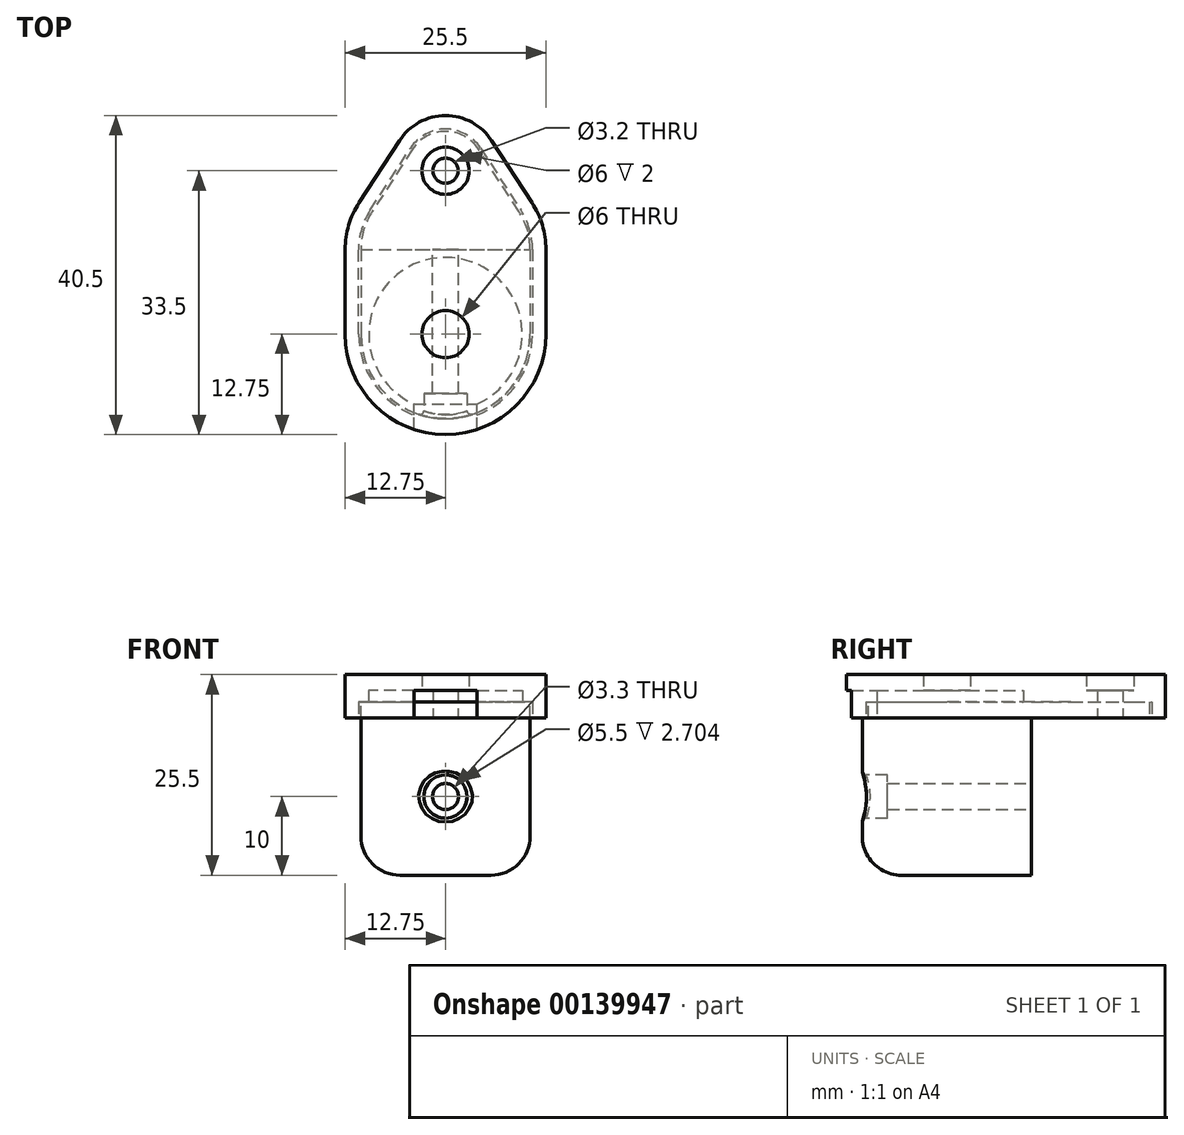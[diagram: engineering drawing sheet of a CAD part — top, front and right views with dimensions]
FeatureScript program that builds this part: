
annotation { "Feature Type Name" : "Feature", "Feature Type Description" : "" }
export const myFeature = defineFeature(function(context is Context, id is Id, definition is map)
    precondition{}
    {
        {
            var Q0;
            Q0=qCreatedBy(makeId("Top.planeOp"),FACE);
            var sketch = newSketch(context, id + "F0", { "sketchPlane" : qUnion([Q0])});
            skCircle(sketch, "E0", {"center": v(0, 0) * mm, "radius": 9.75 * mm, "construction": true});
            skLineSegment(sketch, "E1", {"start": v(-10.75, 10.75) * mm, "end": v(10.75, 10.75) * mm});
            skArc(sketch, "E2", {"start": v(-10.75, 0) * mm, "mid": v(0, -10.75) * mm, "end": v(10.75, 0) * mm});
            skLineSegment(sketch, "E3", {"start": v(-10.75, 10.75) * mm, "end": v(-10.75, 0) * mm});
            skLineSegment(sketch, "E4", {"start": v(10.75, 10.75) * mm, "end": v(10.75, 0) * mm});
            skSolve(sketch);
        }
        {
            var Q0;
            Q0=makeQuery(id+"F0.imprint","IMPRINT",FACE,{"disambiguationData":[TD([[makeQuery(id+"F0.imprint","IMPRINT",EDGE,{"derivedFrom":sQuery(id+"F0.wireOp",EDGE,"E1")}),-1.0]])]});
            extrude(context, id + "F1", {"entities" : qUnion([Q0]), "oppositeDirection" : true, "depth" : 20 * mm});
        }
        {
            var Q0;
            Q0=makeQuery(id+"F1.opExtrude","CAP_FACE",FACE,{"disambiguationData":[OSD([sQuery(id+"F0.wireOp",EDGE,"E1"),sQuery(id+"F0.wireOp",EDGE,"E2"),sQuery(id+"F0.wireOp",EDGE,"E3"),sQuery(id+"F0.wireOp",EDGE,"E4")])],"isStart":true});
            var sketch = newSketch(context, id + "F2", { "sketchPlane" : qUnion([Q0])});
            skArc(sketch, "E5", {"start": v(-10.75, 0) * mm, "mid": v(0, -10.75) * mm, "end": v(10.75, 0) * mm});
            skCircle(sketch, "E6", {"center": v(0, 20.75) * mm, "radius": 1.6 * mm});
            skLineSegment(sketch, "E7", {"start": v(10.75, 0) * mm, "end": v(10.75, 10.75) * mm});
            skLineSegment(sketch, "E8", {"start": v(-10.75, 0) * mm, "end": v(-10.75, 10.75) * mm});
            skArc(sketch, "E9", {"start": v(4.2, 23.47) * mm, "mid": v(0, 25.75) * mm, "end": v(-4.2, 23.47) * mm});
            skArc(sketch, "E10", {"start": v(-9.31, 15.6) * mm, "mid": v(-10.38, 13.28) * mm, "end": v(-10.75, 10.75) * mm});
            skArc(sketch, "E11", {"start": v(10.75, 10.75) * mm, "mid": v(10.38, 13.28) * mm, "end": v(9.31, 15.6) * mm});
            skLineSegment(sketch, "E12", {"start": v(9.31, 15.6) * mm, "end": v(4.2, 23.47) * mm});
            skLineSegment(sketch, "E13", {"start": v(-4.2, 23.47) * mm, "end": v(-9.31, 15.6) * mm});
            skSolve(sketch);
        }
        {
            var Q0;
            Q0 = qSketchRegion(id + "F2", true);
            extrude(context, id + "F3", {"entities" : qUnion([Q0]), "operationType" : NewBodyOperationType.ADD, "depth" : 2 * mm});
        }
        {
            var Q0;
            Q0=makeQuery(id+"F1.opExtrude","SWEPT_FACE",FACE,{"disambiguationData":[OSD([sQuery(id+"F0.wireOp",EDGE,"E1")])]});
            var sketch = newSketch(context, id + "F4", { "sketchPlane" : qUnion([Q0])});
            skCircle(sketch, "E14", {"center": v(0, -10) * mm, "radius": 1.65 * mm});
            skSolve(sketch);
        }
        {
            var Q0;
            Q0 = qSketchRegion(id + "F4", true);
            extrude(context, id + "F5", {"entities" : qUnion([Q0]), "operationType" : NewBodyOperationType.REMOVE, "oppositeDirection" : true, "depth" : 30 * mm});
        }
        {
            var Q0;
            Q0=makeQuery(id+"F1.opExtrude","CAP_EDGE",EDGE,{"disambiguationData":[OSD([sQuery(id+"F0.wireOp",EDGE,"E2")])],"isStart":false});
            cPoint(context, id + "F6", {"entities" : qUnion([Q0]), "parameter" : 0.5});
        }
        {
            var Q0;
            Q0=qCreatedBy(makeId("Front.planeOp"),FACE);
            var Q1;
            Q1 = qCreatedBy(id + "F6" ,VERTEX);
            cPlane(context, id + "F7", {"entities" : qUnion([Q0, Q1]), "cplaneType" : CPlaneType.PLANE_POINT, "offset" : 25 * mm, "width" : 150 * mm, "height" : 150 * mm});
        }
        {
            var Q0;
            Q0=qCreatedBy(id+"F7.planeOp",FACE);
            var sketch = newSketch(context, id + "F8", { "sketchPlane" : qUnion([Q0])});
            skCircle(sketch, "E15", {"center": v(0, -10) * mm, "radius": 2.75 * mm});
            skSolve(sketch);
        }
        {
            var Q0;
            Q0 = qSketchRegion(id + "F8", true);
            extrude(context, id + "F9", {"entities" : qUnion([Q0]), "operationType" : NewBodyOperationType.REMOVE, "oppositeDirection" : true, "depth" : 3.2 * mm});
        }
        {
            var Q0;
            Q0=makeQuery(id+"F9.boolean.opBoolean","INTERSECT",EDGE,{"derivedFrom":[makeQuery(id+"FgSbUSgyND46Qtd_1.boolean.opBoolean","MERGE",FACE,{"derivedFrom":[makeQuery(id+"F3.boolean.opBoolean","MERGE",FACE,{"derivedFrom":[makeQuery(id+"F1.opExtrude","SWEPT_FACE",FACE,{"disambiguationData":[OSD([sQuery(id+"F0.wireOp",EDGE,"E2")])]}),makeQuery(id+"F3.opExtrude","SWEPT_FACE",FACE,{"disambiguationData":[OSD([sQuery(id+"F2.wireOp",EDGE,"do54rNCg-6hwt-ThKP-AdQH-TqJ7PFSLBjPX")])]}),makeQuery(id+"F3.opExtrude","SWEPT_FACE",FACE,{"disambiguationData":[OSD([sQuery(id+"F2.wireOp",EDGE,"E5")])]})]}),makeQuery(id+"FgSbUSgyND46Qtd_1.opExtrude","SWEPT_FACE",FACE,{"disambiguationData":[OSD([sQuery(id+"Fd06qgfGwgJFH88_1.wireOp",EDGE,"OvbUGwiE-2nU8-rEHt-l5LO-rey32bBuKM9T")])]})]}),makeQuery(id+"F9.opExtrude","SWEPT_FACE",FACE,{"disambiguationData":[OSD([sQuery(id+"F8.wireOp",EDGE,"E15")])]})]});
            fillet(context, id + "F10", {"entities" : qUnion([Q0]), "radius" : 0.5 * mm, "tangentPropagation" : true, "allowEdgeOverflow" : false});
        }
        {
            var Q0;
            Q0=makeQuery(id+"F1.opExtrude","CAP_EDGE",EDGE,{"disambiguationData":[OSD([sQuery(id+"F0.wireOp",EDGE,"E2")])],"isStart":false});
            fillet(context, id + "F11", {"entities" : qUnion([Q0]), "radius" : 5 * mm, "tangentPropagation" : true, "allowEdgeOverflow" : false});
        }
        {
            var Q0;
            Q0=qCreatedBy(makeId("Top.planeOp"),FACE);
            var sketch = newSketch(context, id + "F12", { "sketchPlane" : qUnion([Q0])});
            skArc(sketch, "E16", {"start": v(-11.05, 0) * mm, "mid": v(0, -11.05) * mm, "end": v(11.05, 0) * mm});
            skArc(sketch, "E17", {"start": v(-9.57, 15.76) * mm, "mid": v(-10.67, 13.36) * mm, "end": v(-11.05, 10.75) * mm});
            skArc(sketch, "E18", {"start": v(11.05, 10.75) * mm, "mid": v(10.67, 13.36) * mm, "end": v(9.57, 15.76) * mm});
            skArc(sketch, "E19", {"start": v(4.44, 23.64) * mm, "mid": v(0, 26.05) * mm, "end": v(-4.44, 23.64) * mm});
            skLineSegment(sketch, "E20", {"start": v(-11.05, 0) * mm, "end": v(-11.05, 10.75) * mm});
            skLineSegment(sketch, "E21", {"start": v(-9.57, 15.76) * mm, "end": v(-4.44, 23.64) * mm});
            skLineSegment(sketch, "E22", {"start": v(4.44, 23.64) * mm, "end": v(9.57, 15.76) * mm});
            skLineSegment(sketch, "E23", {"start": v(11.05, 10.75) * mm, "end": v(11.05, 0) * mm});
            skArc(sketch, "E24", {"start": v(-12.75, 0) * mm, "mid": v(0, -12.75) * mm, "end": v(12.75, 0) * mm});
            skArc(sketch, "E25", {"start": v(-11, 16.68) * mm, "mid": v(-12.3, 13.84) * mm, "end": v(-12.75, 10.75) * mm});
            skArc(sketch, "E26", {"start": v(12.75, 10.75) * mm, "mid": v(12.3, 13.84) * mm, "end": v(11, 16.68) * mm});
            skArc(sketch, "E27", {"start": v(5.87, 24.56) * mm, "mid": v(0, 27.75) * mm, "end": v(-5.87, 24.56) * mm});
            skLineSegment(sketch, "E28", {"start": v(-12.75, 0) * mm, "end": v(-12.75, 10.75) * mm});
            skLineSegment(sketch, "E29", {"start": v(-11, 16.68) * mm, "end": v(-5.87, 24.56) * mm});
            skLineSegment(sketch, "E30", {"start": v(5.87, 24.56) * mm, "end": v(11, 16.68) * mm});
            skLineSegment(sketch, "E31", {"start": v(12.75, 10.75) * mm, "end": v(12.75, 0) * mm});
            skSolve(sketch);
        }
        {
            var Q0;
            Q0 = qSketchRegion(id + "F12", true);
            extrude(context, id + "F13", {"entities" : qUnion([Q0]), "depth" : 2 * mm});
        }
        {
            var Q0;
            Q0=makeQuery(id+"F13.opExtrude","CAP_FACE",FACE,{"disambiguationData":[OSD([sQuery(id+"F12.wireOp",EDGE,"E16"),sQuery(id+"F12.wireOp",EDGE,"E17"),sQuery(id+"F12.wireOp",EDGE,"E18"),sQuery(id+"F12.wireOp",EDGE,"E19"),sQuery(id+"F12.wireOp",EDGE,"E20"),sQuery(id+"F12.wireOp",EDGE,"E21"),sQuery(id+"F12.wireOp",EDGE,"E22"),sQuery(id+"F12.wireOp",EDGE,"E23"),sQuery(id+"F12.wireOp",EDGE,"E24"),sQuery(id+"F12.wireOp",EDGE,"E25"),sQuery(id+"F12.wireOp",EDGE,"E26"),sQuery(id+"F12.wireOp",EDGE,"E27"),sQuery(id+"F12.wireOp",EDGE,"E28"),sQuery(id+"F12.wireOp",EDGE,"E29"),sQuery(id+"F12.wireOp",EDGE,"E30"),sQuery(id+"F12.wireOp",EDGE,"E31")])],"isStart":false});
            var sketch = newSketch(context, id + "F14", { "sketchPlane" : qUnion([Q0])});
            skCircle(sketch, "E32", {"center": v(0, 20.75) * mm, "radius": 1.6 * mm});
            skArc(sketch, "E33", {"start": v(5.87, 24.56) * mm, "mid": v(0, 27.75) * mm, "end": v(-5.87, 24.56) * mm});
            skArc(sketch, "E34", {"start": v(-11, 16.68) * mm, "mid": v(-12.3, 13.84) * mm, "end": v(-12.75, 10.75) * mm});
            skArc(sketch, "E35", {"start": v(12.75, 10.75) * mm, "mid": v(12.3, 13.84) * mm, "end": v(11, 16.68) * mm});
            skArc(sketch, "E36", {"start": v(-12.75, 0) * mm, "mid": v(-10.33, -7.47) * mm, "end": v(-4, -12.1) * mm});
            skArc(sketch, "E37", {"start": v(4, -12.1) * mm, "mid": v(10.33, -7.47) * mm, "end": v(12.75, 0) * mm});
            skArc(sketch, "E38", {"start": v(4, -8.9) * mm, "mid": v(0, 9.75) * mm, "end": v(-4, -8.9) * mm});
            skLineSegment(sketch, "E39", {"start": v(-4, -12.1) * mm, "end": v(-4, -8.9) * mm});
            skLineSegment(sketch, "E40", {"start": v(4, -12.1) * mm, "end": v(4, -8.9) * mm});
            skLineSegment(sketch, "E41", {"start": v(12.75, 0) * mm, "end": v(12.75, 10.75) * mm});
            skLineSegment(sketch, "E42", {"start": v(11, 16.68) * mm, "end": v(5.87, 24.56) * mm});
            skLineSegment(sketch, "E43", {"start": v(-5.87, 24.56) * mm, "end": v(-11, 16.68) * mm});
            skLineSegment(sketch, "E44", {"start": v(-12.75, 10.75) * mm, "end": v(-12.75, 0) * mm});
            skSolve(sketch);
        }
        {
            var Q0;
            Q0 = qSketchRegion(id + "F14", true);
            extrude(context, id + "F15", {"entities" : qUnion([Q0]), "operationType" : NewBodyOperationType.ADD, "depth" : 1.5 * mm});
        }
        {
            var Q0;
            Q0=makeQuery(id+"F15.opExtrude","CAP_FACE",FACE,{"disambiguationData":[OSD([sQuery(id+"F14.wireOp",EDGE,"E32"),sQuery(id+"F14.wireOp",EDGE,"E33"),sQuery(id+"F14.wireOp",EDGE,"E34"),sQuery(id+"F14.wireOp",EDGE,"E35"),sQuery(id+"F14.wireOp",EDGE,"E36"),sQuery(id+"F14.wireOp",EDGE,"E37"),sQuery(id+"F14.wireOp",EDGE,"E38"),sQuery(id+"F14.wireOp",EDGE,"E39"),sQuery(id+"F14.wireOp",EDGE,"E40"),sQuery(id+"F14.wireOp",EDGE,"E41"),sQuery(id+"F14.wireOp",EDGE,"E42"),sQuery(id+"F14.wireOp",EDGE,"E43"),sQuery(id+"F14.wireOp",EDGE,"E44")])],"isStart":false});
            var sketch = newSketch(context, id + "F16", { "sketchPlane" : qUnion([Q0])});
            skArc(sketch, "E45", {"start": v(5.87, 24.56) * mm, "mid": v(0, 27.75) * mm, "end": v(-5.87, 24.56) * mm});
            skArc(sketch, "E46", {"start": v(-11, 16.68) * mm, "mid": v(-12.3, 13.84) * mm, "end": v(-12.75, 10.75) * mm});
            skArc(sketch, "E47", {"start": v(12.75, 10.75) * mm, "mid": v(12.3, 13.84) * mm, "end": v(11, 16.68) * mm});
            skArc(sketch, "E48", {"start": v(-12.75, 0) * mm, "mid": v(0, -12.75) * mm, "end": v(12.75, 0) * mm});
            skLineSegment(sketch, "E49", {"start": v(-12.75, 0) * mm, "end": v(-12.75, 10.75) * mm});
            skLineSegment(sketch, "E50", {"start": v(-11, 16.68) * mm, "end": v(-5.87, 24.56) * mm});
            skLineSegment(sketch, "E51", {"start": v(5.87, 24.56) * mm, "end": v(11, 16.68) * mm});
            skLineSegment(sketch, "E52", {"start": v(12.75, 10.75) * mm, "end": v(12.75, 0) * mm});
            skCircle(sketch, "E53", {"center": v(0, 20.75) * mm, "radius": 3 * mm});
            skCircle(sketch, "E54", {"center": v(0, 0) * mm, "radius": 3 * mm});
            skSolve(sketch);
        }
        {
            var Q0;
            Q0 = qSketchRegion(id + "F16", true);
            extrude(context, id + "F17", {"entities" : qUnion([Q0]), "operationType" : NewBodyOperationType.ADD, "depth" : 2 * mm});
        }
        {
            var Q0;
            Q0=makeQuery(id+"F12.imprint","IMPRINT",FACE,{"disambiguationData":[TD([[makeQuery(id+"F12.imprint","IMPRINT",EDGE,{"derivedFrom":sQuery(id+"F12.wireOp",EDGE,"E16")}),-1.0]])]});
            var sketch = newSketch(context, id + "F18", { "sketchPlane" : qUnion([Q0])});
            skLineSegment(sketch, "E55.bottom", {"start": v(-4, -13.75) * mm, "end": v(4, -13.75) * mm});
            skLineSegment(sketch, "E55.top", {"start": v(-4, -8.9) * mm, "end": v(4, -8.9) * mm});
            skLineSegment(sketch, "E55.left", {"start": v(-4, -13.75) * mm, "end": v(-4, -8.9) * mm});
            skLineSegment(sketch, "E55.right", {"start": v(4, -13.75) * mm, "end": v(4, -8.9) * mm});
            skSolve(sketch);
        }
        {
            var Q0;
            Q0 = qSketchRegion(id + "F18", true);
            var Q1;
            Q1=makeQuery(id+"F13.opExtrude","CAP_FACE",FACE,{"disambiguationData":[OSD([sQuery(id+"F12.wireOp",EDGE,"E16"),sQuery(id+"F12.wireOp",EDGE,"E17"),sQuery(id+"F12.wireOp",EDGE,"E18"),sQuery(id+"F12.wireOp",EDGE,"E19"),sQuery(id+"F12.wireOp",EDGE,"E20"),sQuery(id+"F12.wireOp",EDGE,"E21"),sQuery(id+"F12.wireOp",EDGE,"E22"),sQuery(id+"F12.wireOp",EDGE,"E23"),sQuery(id+"F12.wireOp",EDGE,"E24"),sQuery(id+"F12.wireOp",EDGE,"E25"),sQuery(id+"F12.wireOp",EDGE,"E26"),sQuery(id+"F12.wireOp",EDGE,"E27"),sQuery(id+"F12.wireOp",EDGE,"E28"),sQuery(id+"F12.wireOp",EDGE,"E29"),sQuery(id+"F12.wireOp",EDGE,"E30"),sQuery(id+"F12.wireOp",EDGE,"E31")])],"isStart":false});
            extrude(context, id + "F19", {"entities" : qUnion([Q0]), "operationType" : NewBodyOperationType.REMOVE, "endBound" : BoundingType.UP_TO_SURFACE, "endBoundEntityFace" : qUnion([Q1]), "depth" : 25 * mm});
        }
    });
